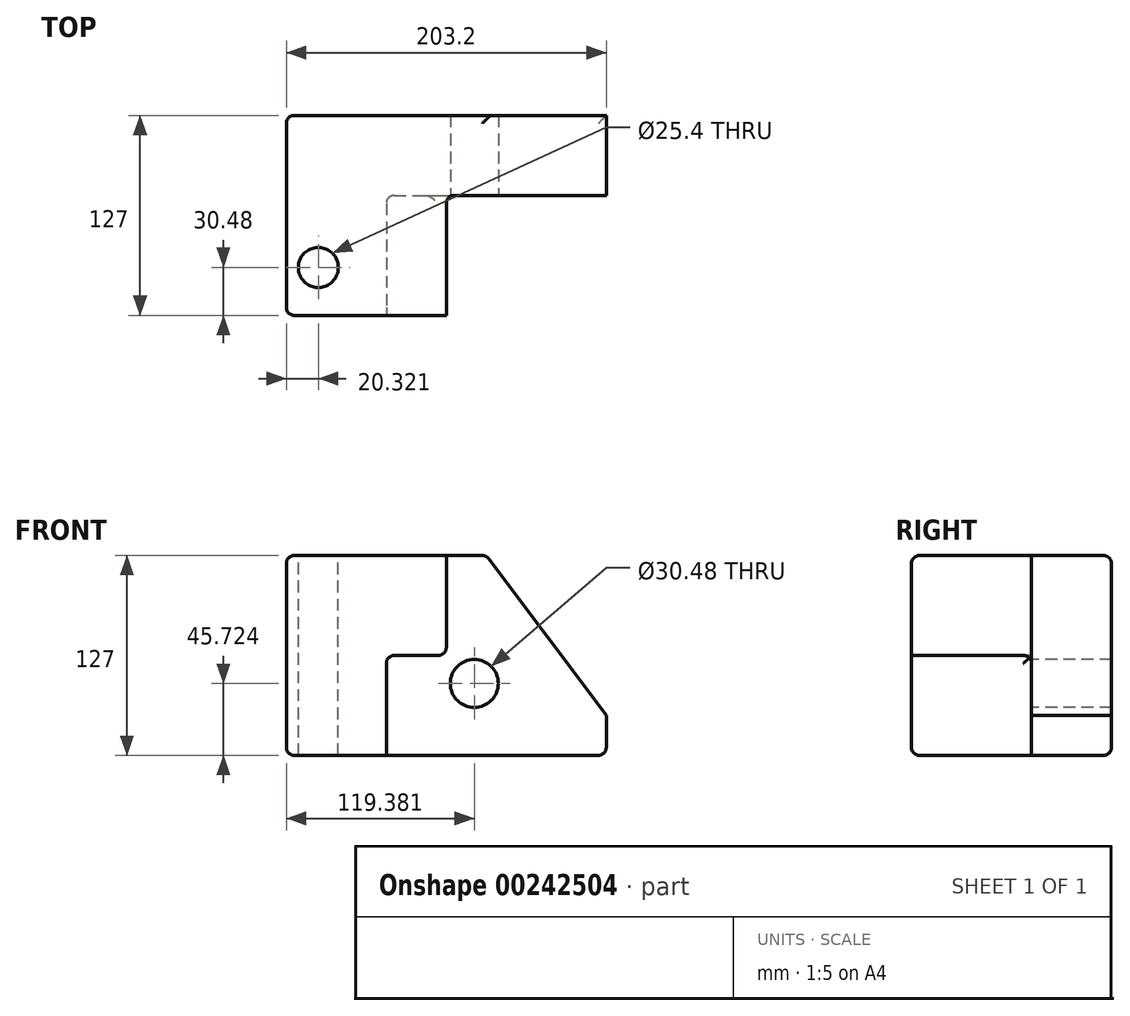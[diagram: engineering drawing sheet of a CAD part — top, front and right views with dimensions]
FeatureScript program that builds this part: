
annotation { "Feature Type Name" : "Feature", "Feature Type Description" : "" }
export const myFeature = defineFeature(function(context is Context, id is Id, definition is map)
    precondition{}
    {
        {
            var Q0;
            Q0=qCreatedBy(makeId("Front.planeOp"),FACE);
            var sketch = newSketch(context, id + "F0", { "sketchPlane" : qUnion([Q0])});
            skLineSegment(sketch, "E0.bottom", {"start": v(-100.69, 58.62) * mm, "end": v(102.51, 58.62) * mm});
            skLineSegment(sketch, "E0.top", {"start": v(-100.69, -68.38) * mm, "end": v(102.51, -68.38) * mm});
            skLineSegment(sketch, "E0.left", {"start": v(-100.69, 58.62) * mm, "end": v(-100.69, -68.38) * mm});
            skLineSegment(sketch, "E0.right", {"start": v(102.51, 58.62) * mm, "end": v(102.51, -68.38) * mm});
            skSolve(sketch);
        }
        {
            var Q0;
            Q0 = qSketchRegion(id + "F0", true);
            extrude(context, id + "F1", {"entities" : qUnion([Q0]), "depth" : 127 * mm});
        }
        {
            var Q0;
            Q0=makeQuery(id+"F1.opExtrude","CAP_FACE",FACE,{"disambiguationData":[OSD([sQuery(id+"F0.wireOp",EDGE,"E0.bottom"),sQuery(id+"F0.wireOp",EDGE,"E0.top"),sQuery(id+"F0.wireOp",EDGE,"E0.left"),sQuery(id+"F0.wireOp",EDGE,"E0.right")])],"isStart":false});
            var sketch = newSketch(context, id + "F2", { "sketchPlane" : qUnion([Q0])});
            skLineSegment(sketch, "E1", {"start": v(-100.69, 58.62) * mm, "end": v(0.91, 58.62) * mm});
            skLineSegment(sketch, "E2", {"start": v(-37.19, -4.88) * mm, "end": v(-37.19, -68.38) * mm});
            skLineSegment(sketch, "E3", {"start": v(-37.19, -68.38) * mm, "end": v(-100.69, -68.38) * mm});
            skLineSegment(sketch, "E4", {"start": v(-100.69, -68.38) * mm, "end": v(-100.69, 58.62) * mm});
            skLineSegment(sketch, "E5", {"start": v(-37.19, -4.88) * mm, "end": v(0.91, -4.88) * mm});
            skLineSegment(sketch, "E6", {"start": v(0.91, -4.88) * mm, "end": v(0.91, 58.62) * mm});
            skSolve(sketch);
        }
        {
            var Q0;
            {var subQ3=sQuery(id+"F2.wireOp",EDGE,"E2");Q0=makeQuery(id+"F2.imprint","IMPRINT",FACE,{"disambiguationData":[TD([[makeQuery(id+"F2.imprint","IMPRINT",EDGE,{"derivedFrom":subQ3}),1.0]])]});}
            extrude(context, id + "F3", {"entities" : qUnion([Q0]), "operationType" : NewBodyOperationType.REMOVE, "oppositeDirection" : true, "depth" : 76.2 * mm});
        }
        {
            var Q0;
            Q0=makeQuery(id+"F1.opExtrude","SWEPT_EDGE",EDGE,{"disambiguationData":[OSD([sQuery(id+"F0.wireOp",EDGE,"E0.bottom"),sQuery(id+"F0.wireOp",EDGE,"E0.right")])]});
            chamfer(context, id + "F4", {"entities" : qUnion([Q0]), "chamferType" : ChamferType.TWO_OFFSETS, "width1" : 76.2 * mm, "oppositeDirection" : false, "width2" : 101.6 * mm, "tangentPropagation" : true});
        }
        {
            var Q0;
            Q0=makeQuery(id+"F3.boolean.opBoolean","COPY",EDGE,{"derivedFrom":makeQuery(id+"F3.opExtrude","SWEPT_EDGE",EDGE,{"disambiguationData":[OSD([sQuery(id+"F0.wireOp",EDGE,"E0.bottom"),sQuery(id+"F2.wireOp",EDGE,"E1"),sQuery(id+"F2.wireOp",EDGE,"E6")])]})});
            var Q1;
            {var subQ0=sQuery(id+"F0.wireOp",EDGE,"E0.bottom");Q1=makeQuery(id+"F4.opChamfer","BLEND_EDGE",EDGE,{"blendedFrom":[makeQuery(id+"F1.opExtrude","SWEPT_EDGE",EDGE,{"disambiguationData":[OSD([subQ0,sQuery(id+"F0.wireOp",EDGE,"E0.right")])]}),makeQuery(id+"F1.opExtrude","SWEPT_FACE",FACE,{"disambiguationData":[OSD([subQ0])]})],"blendedInto":[makeQuery(id+"F1.opExtrude","SWEPT_FACE",FACE,{"disambiguationData":[OSD([subQ0])]})]});}
            var Q2;
            Q2=makeQuery(id+"F3.boolean.opBoolean","COPY",EDGE,{"derivedFrom":makeQuery(id+"F3.opExtrude","CAP_EDGE",EDGE,{"disambiguationData":[OSD([sQuery(id+"F0.wireOp",EDGE,"E0.bottom")])],"isStart":false})});
            var Q3;
            Q3=makeQuery(id+"F1.opExtrude","CAP_EDGE",EDGE,{"disambiguationData":[OSD([sQuery(id+"F0.wireOp",EDGE,"E0.bottom")])],"isStart":false});
            var Q4;
            Q4=makeQuery(id+"F3.boolean.opBoolean","COPY",EDGE,{"derivedFrom":makeQuery(id+"F3.opExtrude","CAP_EDGE",EDGE,{"disambiguationData":[OSD([sQuery(id+"F2.wireOp",EDGE,"E6")])],"isStart":true})});
            var Q5;
            Q5=makeQuery(id+"F3.boolean.opBoolean","COPY",EDGE,{"derivedFrom":makeQuery(id+"F3.opExtrude","SWEPT_EDGE",EDGE,{"disambiguationData":[OSD([sQuery(id+"F2.wireOp",EDGE,"E5"),sQuery(id+"F2.wireOp",EDGE,"E6")])]})});
            var Q6;
            Q6=makeQuery(id+"F3.boolean.opBoolean","COPY",EDGE,{"derivedFrom":makeQuery(id+"F3.opExtrude","CAP_EDGE",EDGE,{"disambiguationData":[OSD([sQuery(id+"F2.wireOp",EDGE,"E5")])],"isStart":true})});
            var Q7;
            Q7=makeQuery(id+"F3.boolean.opBoolean","COPY",EDGE,{"derivedFrom":makeQuery(id+"F3.opExtrude","CAP_EDGE",EDGE,{"disambiguationData":[OSD([sQuery(id+"F2.wireOp",EDGE,"E2")])],"isStart":true})});
            var Q8;
            Q8=makeQuery(id+"F3.boolean.opBoolean","COPY",EDGE,{"derivedFrom":makeQuery(id+"F3.opExtrude","CAP_EDGE",EDGE,{"disambiguationData":[OSD([sQuery(id+"F0.wireOp",EDGE,"E0.top")])],"isStart":false})});
            var Q9;
            Q9=makeQuery(id+"F3.boolean.opBoolean","COPY",EDGE,{"derivedFrom":makeQuery(id+"F3.opExtrude","SWEPT_EDGE",EDGE,{"disambiguationData":[OSD([sQuery(id+"F0.wireOp",EDGE,"E0.top"),sQuery(id+"F2.wireOp",EDGE,"E2"),sQuery(id+"F2.wireOp",EDGE,"E3")])]})});
            var Q10;
            Q10=makeQuery(id+"F1.opExtrude","CAP_EDGE",EDGE,{"disambiguationData":[OSD([sQuery(id+"F0.wireOp",EDGE,"E0.top")])],"isStart":false});
            var Q11;
            Q11=makeQuery(id+"F1.opExtrude","CAP_EDGE",EDGE,{"disambiguationData":[OSD([sQuery(id+"F0.wireOp",EDGE,"E0.left")])],"isStart":false});
            var Q12;
            Q12=makeQuery(id+"F1.opExtrude","SWEPT_EDGE",EDGE,{"disambiguationData":[OSD([sQuery(id+"F0.wireOp",EDGE,"E0.bottom"),sQuery(id+"F0.wireOp",EDGE,"E0.left")])]});
            var Q13;
            Q13=makeQuery(id+"F1.opExtrude","CAP_EDGE",EDGE,{"disambiguationData":[OSD([sQuery(id+"F0.wireOp",EDGE,"E0.bottom")])],"isStart":true});
            var Q14;
            Q14=makeQuery(id+"F1.opExtrude","SWEPT_EDGE",EDGE,{"disambiguationData":[OSD([sQuery(id+"F0.wireOp",EDGE,"E0.top"),sQuery(id+"F0.wireOp",EDGE,"E0.right")])]});
            var Q15;
            Q15=makeQuery(id+"F1.opExtrude","CAP_EDGE",EDGE,{"disambiguationData":[OSD([sQuery(id+"F0.wireOp",EDGE,"E0.left")])],"isStart":true});
            var Q16;
            Q16=makeQuery(id+"F1.opExtrude","SWEPT_EDGE",EDGE,{"disambiguationData":[OSD([sQuery(id+"F0.wireOp",EDGE,"E0.top"),sQuery(id+"F0.wireOp",EDGE,"E0.left")])]});
            var Q17;
            Q17=makeQuery(id+"F1.opExtrude","CAP_EDGE",EDGE,{"disambiguationData":[OSD([sQuery(id+"F0.wireOp",EDGE,"E0.top")])],"isStart":true});
            var Q18;
            Q18=makeQuery(id+"F3.boolean.opBoolean","COPY",EDGE,{"derivedFrom":makeQuery(id+"F3.opExtrude","CAP_EDGE",EDGE,{"disambiguationData":[OSD([sQuery(id+"F2.wireOp",EDGE,"E6")])],"isStart":false})});
            var Q19;
            Q19=makeQuery(id+"F3.boolean.opBoolean","COPY",EDGE,{"derivedFrom":makeQuery(id+"F3.opExtrude","CAP_EDGE",EDGE,{"disambiguationData":[OSD([sQuery(id+"F2.wireOp",EDGE,"E2")])],"isStart":false})});
            var Q20;
            Q20=makeQuery(id+"F3.boolean.opBoolean","COPY",EDGE,{"derivedFrom":makeQuery(id+"F3.opExtrude","SWEPT_EDGE",EDGE,{"disambiguationData":[OSD([sQuery(id+"F2.wireOp",EDGE,"E2"),sQuery(id+"F2.wireOp",EDGE,"E5")])]})});
            fillet(context, id + "F5", {"entities" : qUnion([Q0, Q1, Q2, Q3, Q4, Q5, Q6, Q7, Q8, Q9, Q10, Q11, Q12, Q13, Q14, Q15, Q16, Q17, Q18, Q19, Q20]), "radius" : 5.08 * mm, "tangentPropagation" : true, "allowEdgeOverflow" : false});
        }
        {
            var Q0;
            Q0=makeQuery(id+"F3.boolean.opBoolean","COPY",FACE,{"derivedFrom":makeQuery(id+"F3.opExtrude","CAP_FACE",FACE,{"disambiguationData":[OSD([sQuery(id+"F0.wireOp",EDGE,"E0.bottom"),sQuery(id+"F0.wireOp",EDGE,"E0.top"),sQuery(id+"F0.wireOp",EDGE,"E0.right"),sQuery(id+"F2.wireOp",EDGE,"E2"),sQuery(id+"F2.wireOp",EDGE,"E5"),sQuery(id+"F2.wireOp",EDGE,"E6")])],"isStart":false})});
            var sketch = newSketch(context, id + "F6", { "sketchPlane" : qUnion([Q0])});
            skCircle(sketch, "E7", {"center": v(18.7, -22.66) * mm, "radius": 15.24 * mm});
            skSolve(sketch);
        }
        {
            var Q0;
            Q0=makeQuery(id+"F6.imprint","IMPRINT",FACE,{"disambiguationData":[TD([[makeQuery(id+"F6.imprint","IMPRINT",EDGE,{"derivedFrom":sQuery(id+"F6.wireOp",EDGE,"E7")}),1.0]])]});
            var Q1;
            Q1=makeQuery(id+"F1.opExtrude","CAP_FACE",FACE,{"disambiguationData":[OSD([sQuery(id+"F0.wireOp",EDGE,"E0.bottom"),sQuery(id+"F0.wireOp",EDGE,"E0.top"),sQuery(id+"F0.wireOp",EDGE,"E0.left"),sQuery(id+"F0.wireOp",EDGE,"E0.right")])],"isStart":true});
            extrude(context, id + "F7", {"entities" : qUnion([Q0]), "operationType" : NewBodyOperationType.REMOVE, "endBound" : BoundingType.UP_TO_SURFACE, "oppositeDirection" : true, "endBoundEntityFace" : qUnion([Q1]), "depth" : 25.4 * mm});
        }
        {
            var Q0;
            Q0=makeQuery(id+"F1.opExtrude","SWEPT_FACE",FACE,{"disambiguationData":[OSD([sQuery(id+"F0.wireOp",EDGE,"E0.bottom")])]});
            var sketch = newSketch(context, id + "F8", { "sketchPlane" : qUnion([Q0])});
            skCircle(sketch, "E8", {"center": v(-80.37, -96.52) * mm, "radius": 12.7 * mm});
            skSolve(sketch);
        }
        {
            var Q0;
            Q0=makeQuery(id+"F8.imprint","IMPRINT",FACE,{"disambiguationData":[TD([[makeQuery(id+"F8.imprint","IMPRINT",EDGE,{"derivedFrom":sQuery(id+"F8.wireOp",EDGE,"E8")}),1.0]])]});
            var Q1;
            Q1=makeQuery(id+"F1.opExtrude","SWEPT_FACE",FACE,{"disambiguationData":[OSD([sQuery(id+"F0.wireOp",EDGE,"E0.top")])]});
            extrude(context, id + "F9", {"entities" : qUnion([Q0]), "operationType" : NewBodyOperationType.REMOVE, "endBound" : BoundingType.UP_TO_SURFACE, "oppositeDirection" : true, "endBoundEntityFace" : qUnion([Q1]), "depth" : 25.4 * mm});
        }
    });
